# Revit family: Zalustrowy_podajnik_recznikow_ZZ HIT
name_source: partatom
category: Furniture
units: mm (PartAtom-declared; Revit-internal decimal feet)

## family parameters
Always vertical = Yes
Cut with Voids When Loaded = No
Host = Wall
Room Calculation Point = No
Shared = No

## types (1)
- PZ800SJB
    Depth / Glebokosc = 130 mm  [stored 0.426509 ft]
    Description = Podajnik ręczników papierowych ZZ przeznaczony do montażu za lustrem z możliwością załadunku od dołu. Nowoczesny zalustrowy podajnik ręczników papierowych mogący pomieścić 800 szt listków sprawdza się w designerskich wnętrzach do wszystkich rodzajów podkonstrukcji luster w tym szafek montowanych na stałe bez rewizji.
    Height / Wysokosc = 370 mm  [stored 1.21391 ft]
    Manufacturer = FANECO.com
    Manufacturer code / Kod producenta = 5901764296522
    Material = Stal nierdzewna szczotkowana
    Material finish / Wykonczenie = Stal nierdzewna 430 szczotkowana, mat.
    Model = ZZ HIT
    Product code / Kod produktu = PZ800SJB
    Type Comments = Zalustrowy podajnik ręczników ZZ HIT
    URL = https://faneco.com
    Weight / Waga = 3 kg
    Width / Szerokosc = 290 mm  [stored 0.951444 ft]

note: [stored X ft] marks values corroborated as IEEE doubles in the binary element streams (Revit-internal decimal feet)

## geometry (parser evidence)
native form markers: Sweep x11
no freeform markers — native parametric forms only
